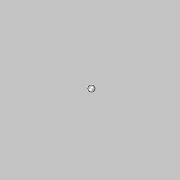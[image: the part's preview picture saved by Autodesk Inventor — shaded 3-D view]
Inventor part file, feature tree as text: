
AUTODESK INVENTOR PART (.ipt)
format: ipt  version: 2017 (Build 210142000, 142)  size: 102,912 bytes
history: native  units: mm
features: other x7, extrude x3, sketch x1, fillet x1
ambient origin geometry x8: Origin, YZ Plane, XZ Plane, XY Plane, X Axis, Y Axis, Z Axis, Center Point
bodies: Solid1 (feature_tree), Solid2 (feature_tree)
feature tree (12):
  other  "Table"
  other  "TL_Armatuur670x70mm"
  other  "TL_Armatuur1260x70mm"
  other  "TL_Armatuur1560x70mm"
  other  "TL_Armatuur670x110mm"
  other  "TL_Armatuur1260x110mm"
  other  "TL_Armatuur1560x110mm"
  sketch  "Sketch1"  dims[d0=5.0mm d2=90.0mm d3=20.0mm d5=0.0mm d8=1550.0mm d9=0.0mm d10=1550.0mm d11=0.0mm d12=20.0mm d14=0.0mm]
  extrude  "Extrusion1"  Depth=90.0mm
  extrude  "Extrusion3"  Depth=20.0mm
  extrude  "Extrusion4"  TaperAngle=0.0deg  [1 undecoded]
  fillet  "Fillet1"  Radius=1550.0mm
note: 1 required parameter value undecoded (feature->parameter linkage not recoverable at this tier; creation-order binding heuristic only, values carry confidence <= 0.55)
